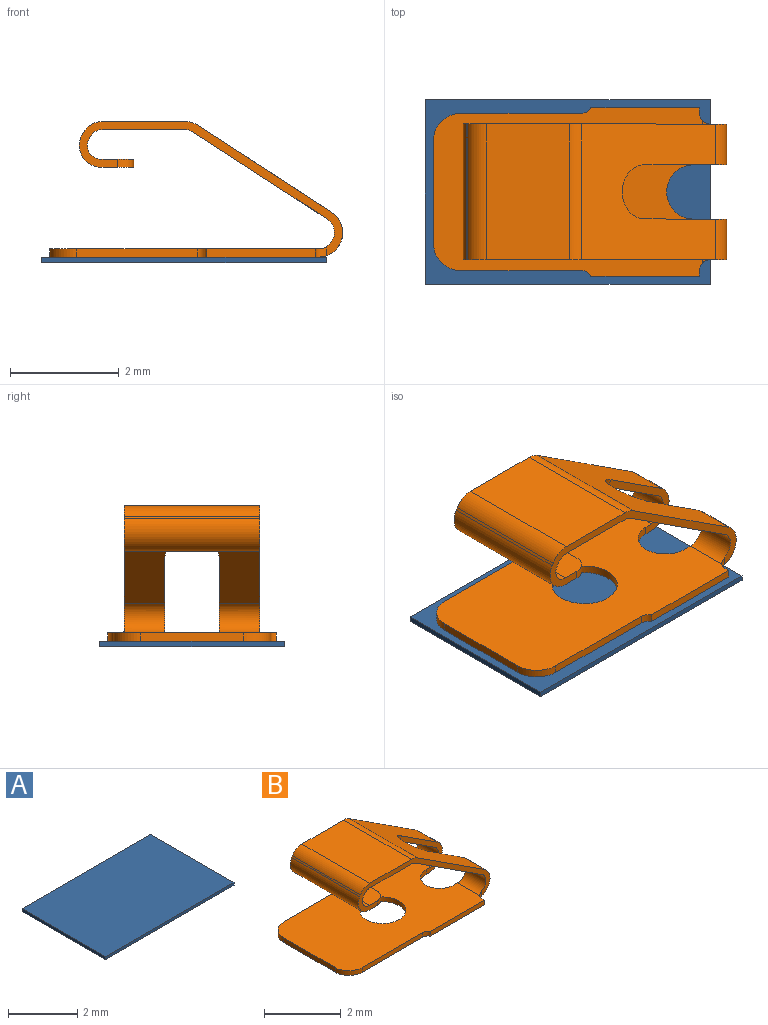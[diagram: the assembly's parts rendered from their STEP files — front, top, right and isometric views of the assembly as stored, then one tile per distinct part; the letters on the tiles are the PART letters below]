
ASSEMBLY  parts=2 mates=1
PART A: 6 faces, bbox 5.3x3.4x0.1 mm
  f0: plane 5.25x0.1mm, normal (0,-1,0), area 0.5mm2, adj f1,f3,f4,f5
  f1: plane 3.4x0.1mm, normal (-1,0,0), area 0.3mm2, adj f0,f2,f4,f5
  f2: plane 5.25x0.1mm, normal (0,1,0), area 0.5mm2, adj f1,f3,f4,f5
  f3: plane 3.4x0.1mm, normal (1,0,0), area 0.3mm2, adj f0,f2,f4,f5
  f4: plane 5.25x3.4mm, normal (0,0,-1), area 17.8mm2, adj f0,f1,f2,f3
  f5: plane 5.25x3.4mm, normal (0,0,1), area 17.8mm2, adj f0,f1,f2,f3
PART B: 43 faces, bbox 5.4x3.1x2.5 mm
  f0: plane 4.95x3.1mm, normal (0,0,-1), area 13mm2, adj f1,f3,f4,f5,f6,f7,f9,f10
  f1: cylinder r=0.6mm len=1.2mm, axis (0,0,1), area 0.6mm2, adj f0,f2
  f2: plane 4.95x3.1mm, normal (0,0,1), area 13mm2, adj f1,f3,f4,f5,f6,f7,f11,f12
  f3: plane 2.23x0.15mm, normal (0,1,0), area 0.3mm2, adj f0,f2,f4,f42
  f4: cylinder r=0.2mm len=0.17mm, axis (0,0,1), area 0mm2, adj f0,f2,f3,f5
  f5: plane 2x0.15mm, normal (0,1,0), area 0.3mm2, adj f0,f2,f4,f6
  f6: plane 0.15x0.1mm, normal (1,0,0), area 0mm2, adj f0,f2,f5,f7
  f7: cylinder r=0.2mm len=0.2mm, axis (0,0,-1), area 0mm2, adj f0,f2,f6,f8,f9,f14
  f8: plane 4.85x2.47mm, normal (0,1,0), area 1mm2, adj f7,f9,f14,f16,f17,f18,f19,f20
  f9: cylinder r=0.45mm len=0.83mm, axis (0,-1,0), area 0.9mm2, adj f0,f7,f8,f11,f32
  f10: cylinder r=0.45mm len=0.83mm, axis (0,-1,0), area 0.9mm2, adj f0,f13,f32,f34,f35
  f11: plane 1.67x1.59mm, normal (0,-1,0), area 0.4mm2, adj f0,f2,f9,f12,f14,f16,f32,f33
  f12: cylinder r=0.5mm len=1mm, axis (0,0,-1), area 0.2mm2, adj f0,f2,f11,f13
  f13: plane 1.67x1.59mm, normal (0,1,0), area 0.4mm2, adj f0,f2,f10,f12,f15,f16,f32,f33
  f14: cylinder r=0.3mm len=0.82mm, axis (0,-1,0), area 0.6mm2, adj f2,f7,f8,f11,f16
  f15: cylinder r=0.3mm len=0.82mm, axis (0,-1,0), area 0.6mm2, adj f2,f13,f16,f34,f35
  f16: plane 2.5x2.47mm, normal (-0.54,0,-0.84), area 5.4mm2, adj f8,f11,f13,f14,f15,f17,f33,f34
  f17: cylinder r=0.25mm len=2.5mm, axis (0,-1,0), area 0.4mm2, adj f8,f16,f18,f34
  f18: plane 2.5x1.53mm, normal (0,0,-1), area 3.8mm2, adj f8,f17,f19,f34
  f19: cylinder r=0.25mm len=2.5mm, axis (0,-1,0), area 0.7mm2, adj f8,f18,f20,f34
  f20: plane 2.5x0.04mm, normal (0.87,0,-0.5), area 0.1mm2, adj f8,f19,f21,f34
  f21: cylinder r=0.25mm len=2.5mm, axis (0,-1,0), area 1.3mm2, adj f8,f20,f22,f34
  f22: plane 2.5x0.6mm, normal (0,0,1), area 1.5mm2, adj f8,f21,f23,f25,f26,f34
  f23: cylinder r=0.3mm len=0.3mm, axis (0,0,-1), area 0.1mm2, adj f22,f24,f25,f34
  f24: plane 2.5x0.6mm, normal (0,0,-1), area 1.5mm2, adj f8,f23,f25,f26,f27,f34
  f25: plane 1.9x0.15mm, normal (1,0,0), area 0.3mm2, adj f22,f23,f24,f26
  f26: cylinder r=0.3mm len=0.3mm, axis (0,0,1), area 0.1mm2, adj f8,f22,f24,f25
  f27: cylinder r=0.4mm len=2.5mm, axis (0,-1,0), area 2.1mm2, adj f8,f24,f28,f34
  f28: plane 2.5x0.04mm, normal (-0.87,0,0.5), area 0.1mm2, adj f8,f27,f29,f34
  f29: cylinder r=0.4mm len=2.5mm, axis (0,-1,0), area 1mm2, adj f8,f28,f30,f34
  f30: plane 2.5x1.53mm, normal (0,0,1), area 3.8mm2, adj f8,f29,f31,f34
  f31: cylinder r=0.4mm len=2.5mm, axis (0,-1,0), area 0.6mm2, adj f8,f30,f32,f34
  f32: plane 2.5x2.47mm, normal (0.54,0,0.84), area 5.4mm2, adj f8,f9,f10,f11,f13,f31,f33,f34
  f33: cylinder r=0.5mm len=1mm, axis (0.54,0,0.84), area 0.2mm2, adj f11,f13,f16,f32
  f34: plane 4.85x2.47mm, normal (0,-1,0), area 1mm2, adj f10,f15,f16,f17,f18,f19,f20,f21
  f35: cylinder r=0.2mm len=0.2mm, axis (0,0,1), area 0mm2, adj f0,f2,f10,f15,f34,f36
  f36: plane 0.15x0.1mm, normal (1,0,0), area 0mm2, adj f0,f2,f35,f37
  f37: plane 2x0.15mm, normal (0,-1,0), area 0.3mm2, adj f0,f2,f36,f38
  f38: cylinder r=0.2mm len=0.17mm, axis (0,0,-1), area 0mm2, adj f0,f2,f37,f39
  f39: plane 2.23x0.15mm, normal (0,-1,0), area 0.3mm2, adj f0,f2,f38,f40
  f40: cylinder r=0.5mm len=0.5mm, axis (0,0,-1), area 0.1mm2, adj f0,f2,f39,f41
  f41: plane 1.9x0.15mm, normal (-1,0,0), area 0.3mm2, adj f0,f2,f40,f42
  f42: cylinder r=0.5mm len=0.5mm, axis (0,0,1), area 0.1mm2, adj f0,f2,f3,f41
PLACE A t=(0.58,0.08,0.48)mm
PLACE B t=(0.58,0.08,0.48)mm
MATE fastened A.f5 <-> B.f0  axis (0,0,1) through (0.35,0.08,0.33)mm
